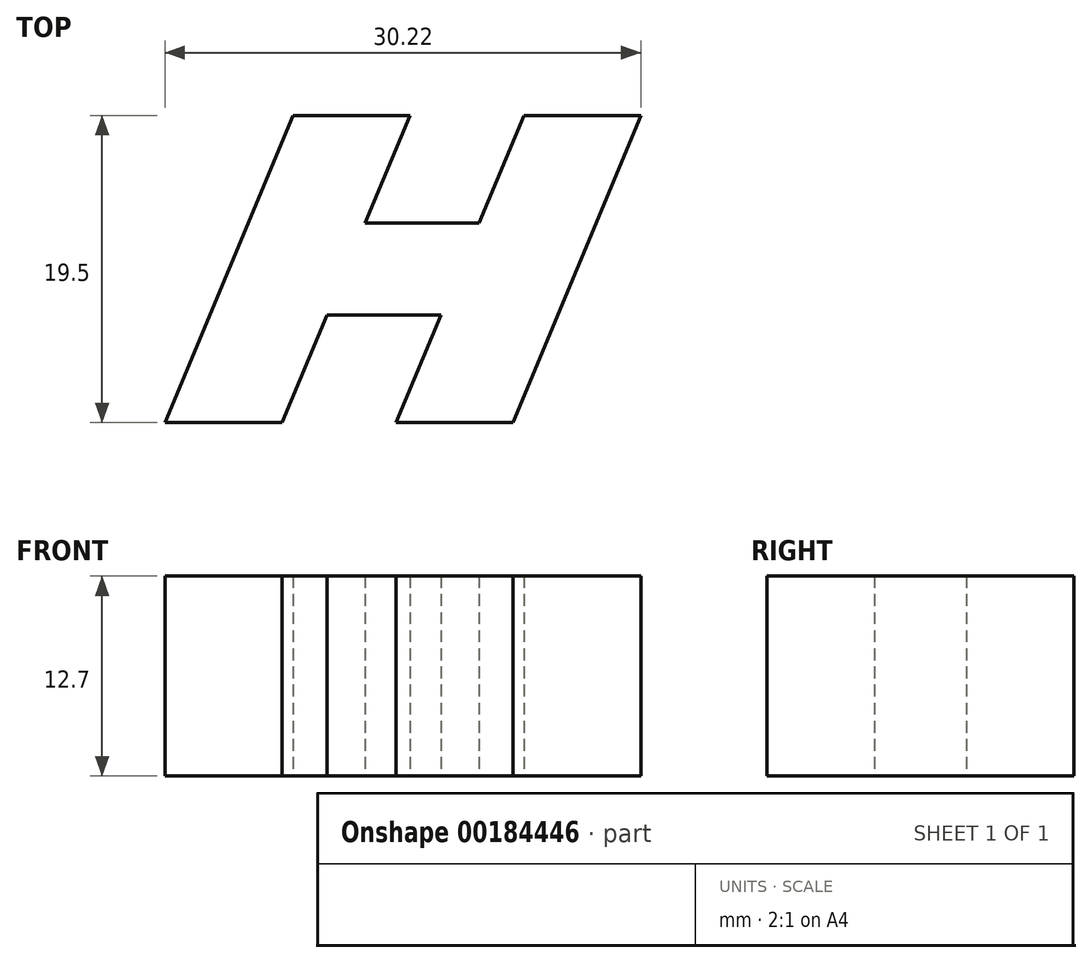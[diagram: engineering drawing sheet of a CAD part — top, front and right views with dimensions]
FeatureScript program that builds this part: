
annotation { "Feature Type Name" : "Feature", "Feature Type Description" : "" }
export const myFeature = defineFeature(function(context is Context, id is Id, definition is map)
    precondition{}
    {
        {
            var Q0;
            Q0=qCreatedBy(makeId("Top.planeOp"),FACE);
            var sketch = newSketch(context, id + "F0", { "sketchPlane" : qUnion([Q0])});
            skLineSegment(sketch, "E0", {"start": v(-38.3, -9.11) * mm, "end": v(-29.76, -9.11) * mm});
            skLineSegment(sketch, "E1", {"start": v(-29.76, 11.4) * mm, "end": v(-38.3, -9.11) * mm});
            skLineSegment(sketch, "E2", {"start": v(-29.76, 11.4) * mm, "end": v(-21.22, 11.4) * mm});
            skLineSegment(sketch, "E3", {"start": v(-6.55, 11.4) * mm, "end": v(-15.1, -9.11) * mm});
            skLineSegment(sketch, "E4", {"start": v(-15.1, -9.11) * mm, "end": v(-23.63, -9.11) * mm});
            skLineSegment(sketch, "E5", {"start": v(-23.63, -9.11) * mm, "end": v(-20.79, -2.28) * mm});
            skLineSegment(sketch, "E6", {"start": v(-29.76, -9.11) * mm, "end": v(-26.92, -2.28) * mm});
            skLineSegment(sketch, "E7", {"start": v(-26.92, -2.28) * mm, "end": v(-20.79, -2.28) * mm});
            skLineSegment(sketch, "E8", {"start": v(-21.22, 11.4) * mm, "end": v(-24.06, 4.58) * mm});
            skLineSegment(sketch, "E9", {"start": v(-24.06, 4.58) * mm, "end": v(-17.93, 4.58) * mm});
            skLineSegment(sketch, "E10.trimOffspring", {"start": v(-24.06, 4.58) * mm, "end": v(-21.22, 11.4) * mm});
            skLineSegment(sketch, "E11.trimOffspring", {"start": v(-17.93, 4.58) * mm, "end": v(-15.1, 11.4) * mm});
            skLineSegment(sketch, "E12.trimOffspring", {"start": v(-15.1, 11.4) * mm, "end": v(-6.55, 11.4) * mm});
            skLineSegment(sketch, "E13.0", {"start": v(-29.42, 10.9) * mm, "end": v(-37.54, -8.6) * mm});
            skLineSegment(sketch, "E13.1", {"start": v(-14.75, 10.9) * mm, "end": v(-7.32, 10.9) * mm});
            skLineSegment(sketch, "E13.2", {"start": v(-17.6, 4.07) * mm, "end": v(-14.75, 10.9) * mm});
            skLineSegment(sketch, "E13.3", {"start": v(-24.83, 4.07) * mm, "end": v(-17.6, 4.07) * mm});
            skLineSegment(sketch, "E13.4", {"start": v(-24.83, 4.07) * mm, "end": v(-21.98, 10.9) * mm});
            skLineSegment(sketch, "E13.5", {"start": v(-7.32, 10.9) * mm, "end": v(-15.43, -8.6) * mm});
            skLineSegment(sketch, "E13.6", {"start": v(-29.42, 10.9) * mm, "end": v(-21.98, 10.9) * mm});
            skLineSegment(sketch, "E13.7", {"start": v(-15.43, -8.6) * mm, "end": v(-22.87, -8.6) * mm});
            skLineSegment(sketch, "E13.8", {"start": v(-22.87, -8.6) * mm, "end": v(-20.03, -1.77) * mm});
            skLineSegment(sketch, "E13.9", {"start": v(-27.26, -1.77) * mm, "end": v(-20.03, -1.77) * mm});
            skLineSegment(sketch, "E13.10", {"start": v(-30.1, -8.6) * mm, "end": v(-27.26, -1.77) * mm});
            skLineSegment(sketch, "E13.11", {"start": v(-37.54, -8.6) * mm, "end": v(-30.1, -8.6) * mm});
            skSolve(sketch);
        }
        {
            var Q0;
            Q0=makeQuery(id+"F0.imprint","IMPRINT",FACE,{"disambiguationData":[TD([[makeQuery(id+"F0.imprint","IMPRINT",EDGE,{"derivedFrom":sQuery(id+"F0.wireOp",EDGE,"E13.0")}),1.0]])]});
            extrude(context, id + "F1", {"entities" : qUnion([Q0]), "depth" : 12.7 * mm});
        }
    });
